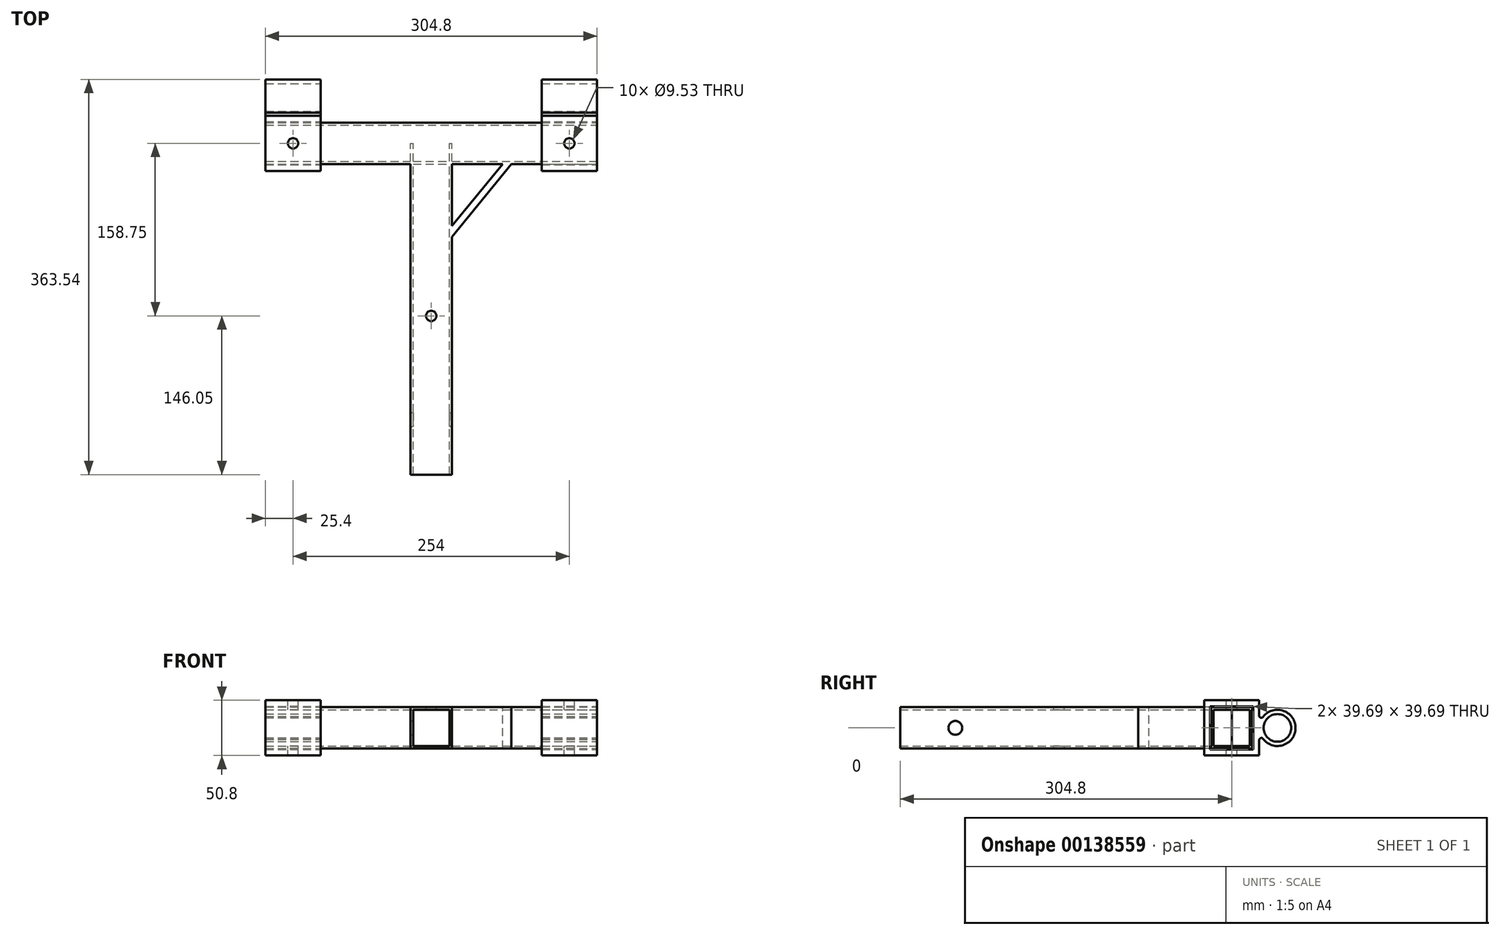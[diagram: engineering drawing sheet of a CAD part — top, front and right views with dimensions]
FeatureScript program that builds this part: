
annotation { "Feature Type Name" : "Feature", "Feature Type Description" : "" }
export const myFeature = defineFeature(function(context is Context, id is Id, definition is map)
    precondition{}
    {
        {
            var Q0;
            Q0=qCreatedBy(makeId("Right.planeOp"),FACE);
            var sketch = newSketch(context, id + "F0", { "sketchPlane" : qUnion([Q0])});
            skLineSegment(sketch, "E0.bottom", {"start": v(16.67, 16.67) * mm, "end": v(-16.67, 16.67) * mm});
            skLineSegment(sketch, "E0.top", {"start": v(16.67, -16.67) * mm, "end": v(-16.67, -16.67) * mm});
            skLineSegment(sketch, "E0.left", {"start": v(16.67, 16.67) * mm, "end": v(16.67, -16.67) * mm});
            skLineSegment(sketch, "E0.right", {"start": v(-16.67, 16.67) * mm, "end": v(-16.67, -16.67) * mm});
            skPoint(sketch, "E0.middle", {"position": v(0, 0) * mm});
            skLineSegment(sketch, "E1.bottom", {"start": v(19.05, 19.05) * mm, "end": v(-19.05, 19.05) * mm});
            skLineSegment(sketch, "E1.top", {"start": v(19.05, -19.05) * mm, "end": v(-19.05, -19.05) * mm});
            skLineSegment(sketch, "E1.left", {"start": v(19.05, 19.05) * mm, "end": v(19.05, -19.05) * mm});
            skLineSegment(sketch, "E1.right", {"start": v(-19.05, 19.05) * mm, "end": v(-19.05, -19.05) * mm});
            skSolve(sketch);
        }
        {
            var Q0;
            Q0 = qSketchRegion(id + "F0", true);
            extrude(context, id + "F1", {"entities" : qUnion([Q0]), "oppositeDirection" : true, "depth" : 304.8 * mm});
        }
        {
            var Q0;
            Q0=qCreatedBy(makeId("Front.planeOp"),FACE);
            var sketch = newSketch(context, id + "F2", { "sketchPlane" : qUnion([Q0])});
            skLineSegment(sketch, "E2.0", {"start": v(-304.8, 19.05) * mm, "end": v(0, 19.05) * mm});
            skLineSegment(sketch, "E3.bottom", {"start": v(-171.45, 19.05) * mm, "end": v(-133.35, 19.05) * mm});
            skLineSegment(sketch, "E3.top", {"start": v(-171.45, -19.05) * mm, "end": v(-133.35, -19.05) * mm});
            skLineSegment(sketch, "E3.left", {"start": v(-171.45, 19.05) * mm, "end": v(-171.45, -19.05) * mm});
            skLineSegment(sketch, "E3.right", {"start": v(-133.35, 19.05) * mm, "end": v(-133.35, -19.05) * mm});
            skPoint(sketch, "E3.middle", {"position": v(-152.4, 0) * mm});
            skPoint(sketch, "E3.middle.positionSnap0", {"position": v(-152.4, 19.05) * mm});
            skPoint(sketch, "E3.centerSnap0", {"position": v(-152.4, 19.05) * mm});
            skLineSegment(sketch, "E4.bottom", {"start": v(-135.73, 16.67) * mm, "end": v(-169.07, 16.67) * mm});
            skLineSegment(sketch, "E4.top", {"start": v(-135.73, -16.67) * mm, "end": v(-169.07, -16.67) * mm});
            skLineSegment(sketch, "E4.left", {"start": v(-135.73, 16.67) * mm, "end": v(-135.73, -16.67) * mm});
            skLineSegment(sketch, "E4.right", {"start": v(-169.07, 16.67) * mm, "end": v(-169.07, -16.67) * mm});
            skSolve(sketch);
        }
        {
            var Q0;
            Q0 = qSketchRegion(id + "F2", true);
            extrude(context, id + "F3", {"entities" : qUnion([Q0]), "operationType" : NewBodyOperationType.ADD, "depth" : 304.8 * mm});
        }
        {
            var Q0;
            Q0=qCreatedBy(makeId("Right.planeOp"),FACE);
            var sketch = newSketch(context, id + "F4", { "sketchPlane" : qUnion([Q0])});
            skLineSegment(sketch, "E5.bottom", {"start": v(19.84, 19.84) * mm, "end": v(-19.84, 19.84) * mm});
            skLineSegment(sketch, "E5.top", {"start": v(19.84, -19.84) * mm, "end": v(-19.84, -19.84) * mm});
            skLineSegment(sketch, "E5.left", {"start": v(19.84, 19.84) * mm, "end": v(19.84, -19.84) * mm});
            skLineSegment(sketch, "E5.right", {"start": v(-19.84, 19.84) * mm, "end": v(-19.84, -19.84) * mm});
            skPoint(sketch, "E5.middle", {"position": v(0, 0) * mm});
            skLineSegment(sketch, "E6.bottom", {"start": v(25.4, 25.4) * mm, "end": v(-25.4, 25.4) * mm});
            skLineSegment(sketch, "E6.top", {"start": v(25.4, -25.4) * mm, "end": v(-25.4, -25.4) * mm});
            skLineSegment(sketch, "E6.left", {"start": v(25.4, 25.4) * mm, "end": v(25.4, -25.4) * mm});
            skLineSegment(sketch, "E6.right", {"start": v(-25.4, 25.4) * mm, "end": v(-25.4, -25.4) * mm});
            skCircle(sketch, "E7", {"center": v(42.07, 0) * mm, "radius": 16.67 * mm});
            skPoint(sketch, "E7.centerSnap0", {"position": v(25.4, 0) * mm});
            skCircle(sketch, "E8", {"center": v(42.07, 0) * mm, "radius": 12.7 * mm});
            skArc(sketch, "E9", {"start": v(25.4, 10.63) * mm, "mid": v(26.57, 9.43) * mm, "end": v(28.24, 9.3) * mm});
            skPoint(sketch, "E9.first.point", {"position": v(25.4, 10.63) * mm});
            skPoint(sketch, "E9.second.point", {"position": v(28.24, 9.3) * mm});
            skPoint(sketch, "E9.third.point", {"position": v(29.93, 11.42) * mm});
            skArc(sketch, "E10.MirrorCS", {"start": v(25.4, -10.63) * mm, "mid": v(26.57, -9.43) * mm, "end": v(28.24, -9.3) * mm});
            skSolve(sketch);
        }
        {
            var Q0;
            Q0 = qSketchRegion(id + "F4", true);
            extrude(context, id + "F5", {"entities" : qUnion([Q0]), "oppositeDirection" : true, "depth" : 50.8 * mm});
        }
        {
            var Q0;
            Q0=makeQuery(id+"F5.opExtrude","SWEPT_BODY",BODY,{"disambiguationData":[OSD([sQuery(id+"F4.wireOp",EDGE,"E5.bottom"),sQuery(id+"F4.wireOp",EDGE,"E5.top"),sQuery(id+"F4.wireOp",EDGE,"E5.left"),sQuery(id+"F4.wireOp",EDGE,"E5.right"),sQuery(id+"F4.wireOp",EDGE,"E6.bottom"),sQuery(id+"F4.wireOp",EDGE,"E6.top"),sQuery(id+"F4.wireOp",EDGE,"E6.left"),sQuery(id+"F4.wireOp",EDGE,"E6.right"),sQuery(id+"F4.wireOp",EDGE,"E7"),sQuery(id+"F4.wireOp",EDGE,"E8"),sQuery(id+"F4.wireOp",EDGE,"E9"),sQuery(id+"F4.wireOp",EDGE,"E10.MirrorCS")])]});
            transform(context, id + "F6", {"entities" : qUnion([Q0]), "transformType" : TransformType.TRANSLATION_3D, "dx" : -254 * mm, "dy" : 0 * mm, "dz" : 0 * mm, "makeCopy" : true});
        }
        {
            var Q0;
            Q0=makeQuery(id+"F5.opExtrude","SWEPT_FACE",FACE,{"disambiguationData":[OSD([sQuery(id+"F4.wireOp",EDGE,"E6.bottom")])]});
            var sketch = newSketch(context, id + "F7", { "sketchPlane" : qUnion([Q0])});
            skLineSegment(sketch, "E11.0", {"start": v(-50.8, -25.4) * mm, "end": v(0, -25.4) * mm});
            skCircle(sketch, "E12", {"center": v(-25.4, 0) * mm, "radius": 4.76 * mm});
            skPoint(sketch, "E12.centerSnap0", {"position": v(-25.4, -25.4) * mm});
            skSolve(sketch);
        }
        {
            var Q0;
            Q0 = qSketchRegion(id + "F7", true);
            extrude(context, id + "F8", {"entities" : qUnion([Q0]), "operationType" : NewBodyOperationType.REMOVE, "endBound" : BoundingType.THROUGH_ALL, "oppositeDirection" : true, "depth" : 50.8 * mm});
        }
        {
            var Q0;
            Q0=makeQuery(id+"F6.opPattern","COPY",FACE,{"derivedFrom":makeQuery(id+"F5.opExtrude","SWEPT_FACE",FACE,{"disambiguationData":[OSD([sQuery(id+"F4.wireOp",EDGE,"E6.bottom")])]}),"instanceName":"1"});
            var sketch = newSketch(context, id + "F9", { "sketchPlane" : qUnion([Q0])});
            skLineSegment(sketch, "E13.0", {"start": v(-304.8, -25.4) * mm, "end": v(-254, -25.4) * mm});
            skLineSegment(sketch, "E14.0", {"start": v(-304.8, 25.4) * mm, "end": v(-304.8, -25.4) * mm});
            skCircle(sketch, "E15", {"center": v(-279.4, 0) * mm, "radius": 4.76 * mm});
            skPoint(sketch, "E15.centerSnap0", {"position": v(-279.4, -25.4) * mm});
            skPoint(sketch, "E15.centerSnap1", {"position": v(-304.8, 0) * mm});
            skSolve(sketch);
        }
        {
            var Q0;
            Q0 = qSketchRegion(id + "F9", true);
            extrude(context, id + "F10", {"entities" : qUnion([Q0]), "operationType" : NewBodyOperationType.REMOVE, "endBound" : BoundingType.THROUGH_ALL, "oppositeDirection" : true, "depth" : 25.4 * mm});
        }
        {
            var Q0;
            {var subQ2=sQuery(id+"F2.wireOp",EDGE,"E3.right");Q0=makeQuery(id+"F3.boolean.opBoolean","SPLIT",FACE,{"disambiguationData":[TD([makeQuery(id+"F1.opExtrude","SWEPT_FACE",FACE,{"disambiguationData":[OSD([sQuery(id+"F0.wireOp",EDGE,"E1.bottom")])]})])],"derivedFrom":makeQuery(id+"F3.opExtrude","SWEPT_FACE",FACE,{"disambiguationData":[OSD([subQ2])]})});}
            var sketch = newSketch(context, id + "F11", { "sketchPlane" : qUnion([Q0])});
            skCircle(sketch, "E16", {"center": v(-254, 0) * mm, "radius": 6.35 * mm});
            skSolve(sketch);
        }
        {
            var Q0;
            Q0 = qSketchRegion(id + "F11", true);
            extrude(context, id + "F12", {"entities" : qUnion([Q0]), "operationType" : NewBodyOperationType.REMOVE, "endBound" : BoundingType.THROUGH_ALL, "oppositeDirection" : true, "depth" : 25.4 * mm});
        }
        {
            var Q0;
            Q0=makeQuery(id+"F3.boolean.opBoolean","MERGE",FACE,{"derivedFrom":[makeQuery(id+"F1.opExtrude","SWEPT_FACE",FACE,{"disambiguationData":[OSD([sQuery(id+"F0.wireOp",EDGE,"E1.bottom")])]}),makeQuery(id+"F3.opExtrude","SWEPT_FACE",FACE,{"disambiguationData":[OSD([sQuery(id+"F2.wireOp",EDGE,"E3.bottom")])]})]});
            var sketch = newSketch(context, id + "F13", { "sketchPlane" : qUnion([Q0])});
            skLineSegment(sketch, "E17", {"start": v(-86.82, -19.05) * mm, "end": v(-133.35, -75.95) * mm});
            skLineSegment(sketch, "E18.0", {"start": v(-78.62, -19.05) * mm, "end": v(-133.35, -85.98) * mm});
            skLineSegment(sketch, "E19", {"start": v(-86.82, -19.05) * mm, "end": v(-78.62, -19.05) * mm});
            skLineSegment(sketch, "E20", {"start": v(-133.35, -75.95) * mm, "end": v(-133.35, -85.98) * mm});
            skSolve(sketch);
        }
        {
            var Q0;
            Q0=qCreatedBy(makeId("Right.planeOp"),FACE);
            cPlane(context, id + "F14", {"entities" : qUnion([Q0]), "cplaneType" : CPlaneType.OFFSET, "offset" : 152.4 * mm, "oppositeDirection" : true, "width" : 152.4 * mm, "height" : 152.4 * mm});
        }
        {
            var Q0;
            Q0=makeQuery(id+"FwdwxloGPFMMXcH_2.1.F13.imprint","IMPRINT",FACE,{"disambiguationData":[TD([[makeQuery(id+"FwdwxloGPFMMXcH_2.1.F13.imprint","IMPRINT",EDGE,{"derivedFrom":sQuery(id+"FwdwxloGPFMMXcH_2.1.F13.wireOp",EDGE,"E17")}),1.0]])]});
            var Q1;
            Q1=makeQuery(id+"F13.imprint","IMPRINT",FACE,{"disambiguationData":[TD([[makeQuery(id+"F13.imprint","IMPRINT",EDGE,{"derivedFrom":sQuery(id+"F13.wireOp",EDGE,"E17")}),1.0]])]});
            extrude(context, id + "F15", {"entities" : qUnion([Q0, Q1]), "operationType" : NewBodyOperationType.ADD, "oppositeDirection" : true, "depth" : 38.1 * mm});
        }
        {
            var Q0;
            Q0=makeQuery(id+"F15.boolean.opBoolean","MERGE",FACE,{"derivedFrom":[makeQuery(id+"F3.boolean.opBoolean","MERGE",FACE,{"derivedFrom":[makeQuery(id+"F1.opExtrude","SWEPT_FACE",FACE,{"disambiguationData":[OSD([sQuery(id+"F0.wireOp",EDGE,"E1.bottom")])]}),makeQuery(id+"F3.opExtrude","SWEPT_FACE",FACE,{"disambiguationData":[OSD([sQuery(id+"F2.wireOp",EDGE,"E3.bottom")])]})]}),makeQuery(id+"F15.opExtrude","CAP_FACE",FACE,{"disambiguationData":[OSD([sQuery(id+"F13.wireOp",EDGE,"E17"),sQuery(id+"F13.wireOp",EDGE,"E18.0"),sQuery(id+"F13.wireOp",EDGE,"E19"),sQuery(id+"F13.wireOp",EDGE,"E20")])],"isStart":true}),makeQuery(id+"F15.opExtrude","CAP_FACE",FACE,{"disambiguationData":[OSD([sQuery(id+"FwdwxloGPFMMXcH_2.1.F13.wireOp",EDGE,"E17"),sQuery(id+"FwdwxloGPFMMXcH_2.1.F13.wireOp",EDGE,"E18.0"),sQuery(id+"FwdwxloGPFMMXcH_2.1.F13.wireOp",EDGE,"E19"),sQuery(id+"FwdwxloGPFMMXcH_2.1.F13.wireOp",EDGE,"E20")])],"isStart":true})]});
            var sketch = newSketch(context, id + "F16", { "sketchPlane" : qUnion([Q0])});
            skCircle(sketch, "E21", {"center": v(-152.4, -158.75) * mm, "radius": 4.76 * mm});
            skPoint(sketch, "E21.centerSnap0", {"position": v(-152.4, 19.05) * mm});
            skSolve(sketch);
        }
        {
            var Q0;
            Q0 = qSketchRegion(id + "F16", true);
            extrude(context, id + "F17", {"entities" : qUnion([Q0]), "operationType" : NewBodyOperationType.REMOVE, "endBound" : BoundingType.THROUGH_ALL, "oppositeDirection" : true, "depth" : 25.4 * mm});
        }
    });
